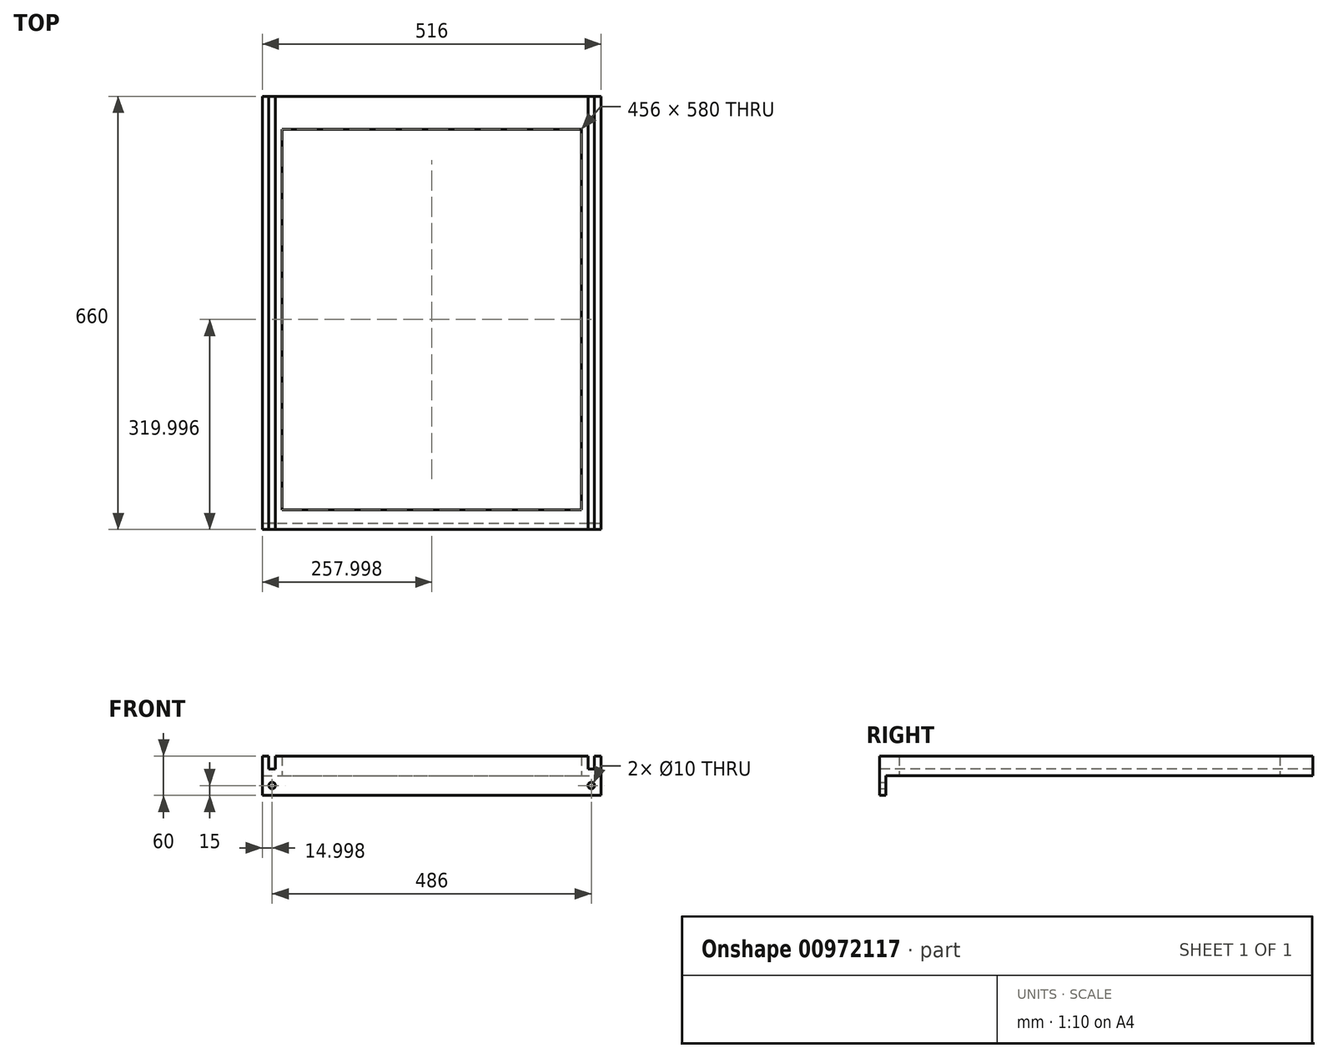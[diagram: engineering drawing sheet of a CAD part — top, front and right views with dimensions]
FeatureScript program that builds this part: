
annotation { "Feature Type Name" : "Feature", "Feature Type Description" : "" }
export const myFeature = defineFeature(function(context is Context, id is Id, definition is map)
    precondition{}
    {
        {
            var Q0;
            Q0=qCreatedBy(makeId("Top.planeOp"),FACE);
            var sketch = newSketch(context, id + "F0", { "sketchPlane" : qUnion([Q0])});
            skLineSegment(sketch, "E0.bottom", {"start": v(-227.04, 462.19) * mm, "end": v(288.96, 462.19) * mm});
            skLineSegment(sketch, "E0.top", {"start": v(-227.04, -197.81) * mm, "end": v(288.96, -197.81) * mm});
            skLineSegment(sketch, "E0.left", {"start": v(-227.04, 462.19) * mm, "end": v(-227.04, -197.81) * mm});
            skLineSegment(sketch, "E0.right", {"start": v(288.96, 462.19) * mm, "end": v(288.96, -197.81) * mm});
            skLineSegment(sketch, "E1.bottom", {"start": v(-197.04, 412.19) * mm, "end": v(258.96, 412.19) * mm});
            skLineSegment(sketch, "E1.top", {"start": v(-197.04, -167.81) * mm, "end": v(258.96, -167.81) * mm});
            skLineSegment(sketch, "E1.left", {"start": v(-197.04, 412.19) * mm, "end": v(-197.04, -167.81) * mm});
            skLineSegment(sketch, "E1.right", {"start": v(258.96, 412.19) * mm, "end": v(258.96, -167.81) * mm});
            skSolve(sketch);
        }
        {
            var Q0;
            Q0=makeQuery(id+"F0.imprint","IMPRINT",FACE,{"disambiguationData":[TD([[makeQuery(id+"F0.imprint","IMPRINT",EDGE,{"derivedFrom":sQuery(id+"F0.wireOp",EDGE,"E0.bottom")}),-1.0]])]});
            extrude(context, id + "F1", {"entities" : qUnion([Q0]), "depth" : 20 * mm, "offsetDistance" : 25 * mm});
        }
        {
            var Q0;
            Q0=makeQuery(id+"F1.opExtrude","CAP_FACE",FACE,{"disambiguationData":[OSD([sQuery(id+"F0.wireOp",EDGE,"E0.bottom"),sQuery(id+"F0.wireOp",EDGE,"E0.top"),sQuery(id+"F0.wireOp",EDGE,"E0.left"),sQuery(id+"F0.wireOp",EDGE,"E0.right"),sQuery(id+"F0.wireOp",EDGE,"E1.bottom"),sQuery(id+"F0.wireOp",EDGE,"E1.top"),sQuery(id+"F0.wireOp",EDGE,"E1.left"),sQuery(id+"F0.wireOp",EDGE,"E1.right")])],"isStart":false});
            var sketch = newSketch(context, id + "F2", { "sketchPlane" : qUnion([Q0])});
            skLineSegment(sketch, "E2.bottom", {"start": v(-217.04, -197.81) * mm, "end": v(-207.04, -197.81) * mm});
            skLineSegment(sketch, "E2.top", {"start": v(-217.04, 462.19) * mm, "end": v(-207.04, 462.19) * mm});
            skLineSegment(sketch, "E2.left", {"start": v(-217.04, -197.81) * mm, "end": v(-217.04, 462.19) * mm});
            skLineSegment(sketch, "E2.right", {"start": v(-207.04, -197.81) * mm, "end": v(-207.04, 462.19) * mm});
            skLineSegment(sketch, "E3.bottom", {"start": v(268.96, 462.19) * mm, "end": v(278.96, 462.19) * mm});
            skLineSegment(sketch, "E3.top", {"start": v(268.96, -197.81) * mm, "end": v(278.96, -197.81) * mm});
            skLineSegment(sketch, "E3.left", {"start": v(268.96, 462.19) * mm, "end": v(268.96, -197.81) * mm});
            skLineSegment(sketch, "E3.right", {"start": v(278.96, 462.19) * mm, "end": v(278.96, -197.81) * mm});
            skSolve(sketch);
        }
        {
            var Q0;
            Q0 = qSketchRegion(id + "F2", true);
            extrude(context, id + "F3", {"entities" : qUnion([Q0]), "operationType" : NewBodyOperationType.REMOVE, "oppositeDirection" : true, "depth" : 10 * mm, "offsetDistance" : 25 * mm});
        }
        {
            var Q0;
            {var subQ0=sQuery(id+"F0.wireOp",EDGE,"E0.bottom");var subQ1=sQuery(id+"F0.wireOp",EDGE,"E0.right");var subQ2=sQuery(id+"F0.wireOp",EDGE,"E0.top");Q0=makeQuery(id+"F3.boolean.opBoolean","SPLIT",FACE,{"disambiguationData":[TD([makeQuery(id+"F1.opExtrude","SWEPT_FACE",FACE,{"disambiguationData":[OSD([subQ1])]})])],"derivedFrom":makeQuery(id+"F1.opExtrude","CAP_FACE",FACE,{"disambiguationData":[OSD([subQ0,subQ2,sQuery(id+"F0.wireOp",EDGE,"E0.left"),subQ1,sQuery(id+"F0.wireOp",EDGE,"E1.bottom"),sQuery(id+"F0.wireOp",EDGE,"E1.top"),sQuery(id+"F0.wireOp",EDGE,"E1.left"),sQuery(id+"F0.wireOp",EDGE,"E1.right")])],"isStart":false})});}
            var Q1;
            {var subQ0=sQuery(id+"F0.wireOp",EDGE,"E0.bottom");var subQ1=sQuery(id+"F0.wireOp",EDGE,"E0.top");var subQ2=sQuery(id+"F0.wireOp",EDGE,"E0.left");Q1=makeQuery(id+"F3.boolean.opBoolean","SPLIT",FACE,{"disambiguationData":[TD([makeQuery(id+"F1.opExtrude","SWEPT_FACE",FACE,{"disambiguationData":[OSD([subQ2])]})])],"derivedFrom":makeQuery(id+"F1.opExtrude","CAP_FACE",FACE,{"disambiguationData":[OSD([subQ0,subQ1,subQ2,sQuery(id+"F0.wireOp",EDGE,"E0.right"),sQuery(id+"F0.wireOp",EDGE,"E1.bottom"),sQuery(id+"F0.wireOp",EDGE,"E1.top"),sQuery(id+"F0.wireOp",EDGE,"E1.left"),sQuery(id+"F0.wireOp",EDGE,"E1.right")])],"isStart":false})});}
            var Q2;
            {var subQ0=sQuery(id+"F0.wireOp",EDGE,"E1.top");var subQ1=sQuery(id+"F0.wireOp",EDGE,"E1.bottom");var subQ2=sQuery(id+"F0.wireOp",EDGE,"E0.top");var subQ3=sQuery(id+"F0.wireOp",EDGE,"E0.bottom");var subQ4=sQuery(id+"F0.wireOp",EDGE,"E1.left");var subQ5=sQuery(id+"F0.wireOp",EDGE,"E1.right");Q2=makeQuery(id+"F3.boolean.opBoolean","SPLIT",FACE,{"disambiguationData":[TD([makeQuery(id+"F1.opExtrude","SWEPT_FACE",FACE,{"disambiguationData":[OSD([subQ1])]})])],"derivedFrom":makeQuery(id+"F1.opExtrude","CAP_FACE",FACE,{"disambiguationData":[OSD([subQ3,subQ2,sQuery(id+"F0.wireOp",EDGE,"E0.left"),sQuery(id+"F0.wireOp",EDGE,"E0.right"),subQ1,subQ0,subQ4,subQ5])],"isStart":false})});}
            extrude(context, id + "F4", {"entities" : qUnion([Q0, Q1, Q2]), "operationType" : NewBodyOperationType.ADD, "depth" : 10 * mm, "offsetDistance" : 25 * mm});
        }
        {
            var Q0;
            Q0=makeQuery(id+"F1.opExtrude","CAP_FACE",FACE,{"disambiguationData":[OSD([sQuery(id+"F0.wireOp",EDGE,"E0.bottom"),sQuery(id+"F0.wireOp",EDGE,"E0.top"),sQuery(id+"F0.wireOp",EDGE,"E0.left"),sQuery(id+"F0.wireOp",EDGE,"E0.right"),sQuery(id+"F0.wireOp",EDGE,"E1.bottom"),sQuery(id+"F0.wireOp",EDGE,"E1.top"),sQuery(id+"F0.wireOp",EDGE,"E1.left"),sQuery(id+"F0.wireOp",EDGE,"E1.right")])],"isStart":true});
            var sketch = newSketch(context, id + "F5", { "sketchPlane" : qUnion([Q0])});
            skLineSegment(sketch, "E4.bottom", {"start": v(-227.04, 197.81) * mm, "end": v(-197.04, 197.81) * mm});
            skLineSegment(sketch, "E4.top", {"start": v(-227.04, 187.81) * mm, "end": v(-197.04, 187.81) * mm});
            skLineSegment(sketch, "E4.left", {"start": v(-227.04, 197.81) * mm, "end": v(-227.04, 187.81) * mm});
            skLineSegment(sketch, "E4.right", {"start": v(-197.04, 197.81) * mm, "end": v(-197.04, 187.81) * mm});
            skLineSegment(sketch, "E5.bottom", {"start": v(288.96, 197.81) * mm, "end": v(258.96, 197.81) * mm});
            skLineSegment(sketch, "E5.top", {"start": v(288.96, 187.81) * mm, "end": v(258.96, 187.81) * mm});
            skLineSegment(sketch, "E5.left", {"start": v(288.96, 197.81) * mm, "end": v(288.96, 187.81) * mm});
            skLineSegment(sketch, "E5.right", {"start": v(258.96, 197.81) * mm, "end": v(258.96, 187.81) * mm});
            skSolve(sketch);
        }
        {
            var Q0;
            Q0=makeQuery(id+"F5.imprint","IMPRINT",FACE,{"disambiguationData":[TD([[makeQuery(id+"F5.imprint","IMPRINT",EDGE,{"derivedFrom":sQuery(id+"F5.wireOp",EDGE,"E5.bottom")}),-1.0]])]});
            var Q1;
            Q1=makeQuery(id+"F5.imprint","IMPRINT",FACE,{"disambiguationData":[TD([[makeQuery(id+"F5.imprint","IMPRINT",EDGE,{"derivedFrom":sQuery(id+"F5.wireOp",EDGE,"E4.bottom")}),-1.0]])]});
            extrude(context, id + "F6", {"entities" : qUnion([Q0, Q1]), "operationType" : NewBodyOperationType.ADD, "depth" : 30 * mm, "offsetDistance" : 25 * mm});
        }
        {
            var Q0;
            Q0=makeQuery(id+"F6.opExtrude","SWEPT_FACE",FACE,{"disambiguationData":[OSD([sQuery(id+"F5.wireOp",EDGE,"E4.top")])]});
            var sketch = newSketch(context, id + "F7", { "sketchPlane" : qUnion([Q0])});
            skPoint(sketch, "E6", {"position": v(212.04, -15) * mm});
            skPoint(sketch, "E6.positionSnap0", {"position": v(197.04, -15) * mm});
            skPoint(sketch, "E6.positionSnap1", {"position": v(212.04, -30) * mm});
            skPoint(sketch, "E7", {"position": v(-273.96, -15) * mm});
            skSolve(sketch);
        }
        {
            var Q0;
            Q0=sQuery(id+"F7.wireOp",VERTEX,"E6");
            var Q1;
            Q1=sQuery(id+"F7.wireOp",VERTEX,"E7");
            var Q2;
            Q2=makeQuery(id+"F1.opExtrude","SWEPT_BODY",BODY,{"disambiguationData":[OSD([sQuery(id+"F0.wireOp",EDGE,"E0.bottom"),sQuery(id+"F0.wireOp",EDGE,"E0.top"),sQuery(id+"F0.wireOp",EDGE,"E0.left"),sQuery(id+"F0.wireOp",EDGE,"E0.right"),sQuery(id+"F0.wireOp",EDGE,"E1.bottom"),sQuery(id+"F0.wireOp",EDGE,"E1.top"),sQuery(id+"F0.wireOp",EDGE,"E1.left"),sQuery(id+"F0.wireOp",EDGE,"E1.right")])]});
            hole(context, id + "F8", {"style" : HoleStyle.SIMPLE, "endStyle" : HoleEndStyle.THROUGH, "holeDiameter" : 10 * mm, "majorDiameter" : 5 * mm, "isTappedThrough" : true, "tappedDepth" : 12 * mm, "tapClearance" : 3, "locations" : qUnion([Q0, Q1]), "scope" : qUnion([Q2])});
        }
        {
            var Q0;
            Q0=makeQuery(id+"F6.opExtrude","SWEPT_FACE",FACE,{"disambiguationData":[OSD([sQuery(id+"F5.wireOp",EDGE,"E5.right")])]});
            extrude(context, id + "F9", {"entities" : qUnion([Q0]), "operationType" : NewBodyOperationType.ADD, "endBound" : BoundingType.UP_TO_NEXT, "depth" : 25 * mm, "offsetDistance" : 25 * mm});
        }
    });
